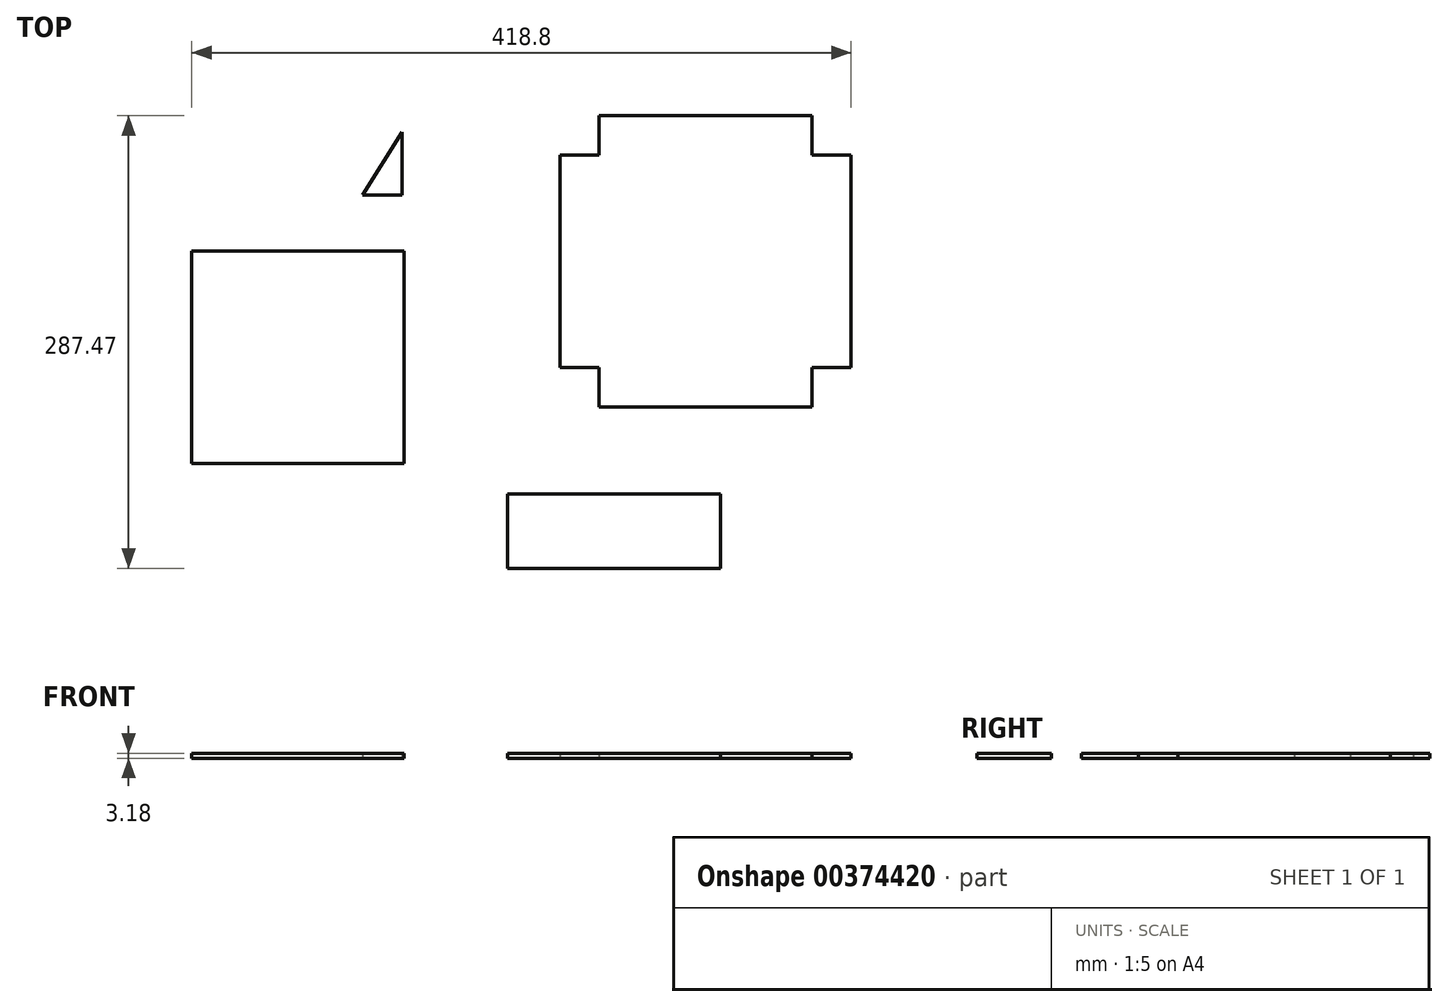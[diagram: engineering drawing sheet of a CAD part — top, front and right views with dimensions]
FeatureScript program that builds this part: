
annotation { "Feature Type Name" : "Feature", "Feature Type Description" : "" }
export const myFeature = defineFeature(function(context is Context, id is Id, definition is map)
    precondition{}
    {
        {
            var Q0;
            Q0=qCreatedBy(makeId("Top.planeOp"),FACE);
            var sketch = newSketch(context, id + "F0", { "sketchPlane" : qUnion([Q0])});
            skLineSegment(sketch, "E0.bottom", {"start": v(41.52, 76.38) * mm, "end": v(-93.48, 76.38) * mm});
            skLineSegment(sketch, "E0.top", {"start": v(41.52, -58.62) * mm, "end": v(-93.48, -58.62) * mm});
            skLineSegment(sketch, "E0.left", {"start": v(41.52, 76.38) * mm, "end": v(41.52, -58.62) * mm});
            skLineSegment(sketch, "E0.right", {"start": v(-93.48, 76.38) * mm, "end": v(-93.48, -58.62) * mm});
            skPoint(sketch, "E0.middle", {"position": v(-25.98, 8.88) * mm});
            skLineSegment(sketch, "E1.bottom", {"start": v(325.32, 162.44) * mm, "end": v(140.32, 162.44) * mm});
            skLineSegment(sketch, "E1.top", {"start": v(325.32, -22.56) * mm, "end": v(140.32, -22.56) * mm});
            skLineSegment(sketch, "E1.left", {"start": v(325.32, 162.44) * mm, "end": v(325.32, -22.56) * mm});
            skLineSegment(sketch, "E1.right", {"start": v(140.32, 162.44) * mm, "end": v(140.32, -22.56) * mm});
            skPoint(sketch, "E1.middle", {"position": v(232.82, 69.94) * mm});
            skLineSegment(sketch, "E2", {"start": v(40.03, 152.07) * mm, "end": v(40.03, 112.07) * mm});
            skLineSegment(sketch, "E3", {"start": v(40.03, 112.07) * mm, "end": v(15.03, 112.07) * mm});
            skLineSegment(sketch, "E4", {"start": v(15.03, 112.07) * mm, "end": v(40.03, 152.07) * mm});
            skLineSegment(sketch, "E5.bottom", {"start": v(107.2, -77.86) * mm, "end": v(242.2, -77.86) * mm});
            skLineSegment(sketch, "E5.top", {"start": v(107.2, -125.03) * mm, "end": v(242.2, -125.03) * mm});
            skLineSegment(sketch, "E5.left", {"start": v(107.2, -77.86) * mm, "end": v(107.2, -125.03) * mm});
            skLineSegment(sketch, "E5.right", {"start": v(242.2, -77.86) * mm, "end": v(242.2, -125.03) * mm});
            skLineSegment(sketch, "E6", {"start": v(165.32, -22.56) * mm, "end": v(165.32, 2.44) * mm});
            skLineSegment(sketch, "E7", {"start": v(165.32, 2.44) * mm, "end": v(140.32, 2.44) * mm});
            skLineSegment(sketch, "E8", {"start": v(140.32, 69.94) * mm, "end": v(325.32, 69.94) * mm});
            skLineSegment(sketch, "E9", {"start": v(232.82, 162.44) * mm, "end": v(232.82, -22.56) * mm});
            skLineSegment(sketch, "E10.MirrorCS", {"start": v(165.32, 137.44) * mm, "end": v(140.32, 137.44) * mm});
            skLineSegment(sketch, "E11.MirrorCS", {"start": v(165.32, 162.44) * mm, "end": v(165.32, 137.44) * mm});
            skLineSegment(sketch, "E12.MirrorCS", {"start": v(300.32, 162.44) * mm, "end": v(300.32, 137.44) * mm});
            skLineSegment(sketch, "E13.MirrorCS", {"start": v(300.32, 137.44) * mm, "end": v(325.32, 137.44) * mm});
            skLineSegment(sketch, "E14.MirrorCS", {"start": v(300.32, 2.44) * mm, "end": v(325.32, 2.44) * mm});
            skLineSegment(sketch, "E15.MirrorCS", {"start": v(300.32, -22.56) * mm, "end": v(300.32, 2.44) * mm});
            skSolve(sketch);
        }
        {
            var Q0;
            Q0=makeQuery(id+"F0.imprint","IMPRINT",FACE,{"disambiguationData":[TD([[makeQuery(id+"F0.imprint","IMPRINT",EDGE,{"derivedFrom":sQuery(id+"F0.wireOp",EDGE,"E0.bottom")}),1.0]])]});
            var Q1;
            Q1=makeQuery(id+"F0.imprint","IMPRINT",FACE,{"disambiguationData":[TD([[makeQuery(id+"F0.imprint","IMPRINT",EDGE,{"derivedFrom":sQuery(id+"F0.wireOp",EDGE,"E2")}),-1.0]])]});
            var Q2;
            Q2=makeQuery(id+"F0.imprint","IMPRINT",FACE,{"disambiguationData":[TD([[makeQuery(id+"F0.imprint","IMPRINT",EDGE,{"derivedFrom":sQuery(id+"F0.wireOp",EDGE,"E5.bottom")}),-1.0]])]});
            var Q3;
            {var subQ5=sQuery(id+"F0.wireOp",EDGE,"E10.MirrorCS");Q3=makeQuery(id+"F0.imprint","IMPRINT",FACE,{"disambiguationData":[TD([[makeQuery(id+"F0.imprint","IMPRINT",EDGE,{"derivedFrom":subQ5}),1.0]])]});}
            var Q4;
            {var subQ0=sQuery(id+"F0.wireOp",EDGE,"E6");Q4=makeQuery(id+"F0.imprint","IMPRINT",FACE,{"disambiguationData":[TD([[makeQuery(id+"F0.imprint","IMPRINT",EDGE,{"derivedFrom":subQ0}),-1.0]])]});}
            var Q5;
            {var subQ7=sQuery(id+"F0.wireOp",EDGE,"E14.MirrorCS");Q5=makeQuery(id+"F0.imprint","IMPRINT",FACE,{"disambiguationData":[TD([[makeQuery(id+"F0.imprint","IMPRINT",EDGE,{"derivedFrom":subQ7}),1.0]])]});}
            var Q6;
            {var subQ8=sQuery(id+"F0.wireOp",EDGE,"E12.MirrorCS");Q6=makeQuery(id+"F0.imprint","IMPRINT",FACE,{"disambiguationData":[TD([[makeQuery(id+"F0.imprint","IMPRINT",EDGE,{"derivedFrom":subQ8}),-1.0]])]});}
            extrude(context, id + "F1", {"entities" : qUnion([Q0, Q1, Q2, Q3, Q4, Q5, Q6]), "depth" : 3.18 * mm});
        }
    });
